annotation { "Feature Type Name" : "Feature", "Feature Type Description" : "" }
export const myFeature = defineFeature(function(context is Context, id is Id, definition is map)
    precondition{}
    {
        {
            var Q0;
            Q0=qCreatedBy(makeId("Front.planeOp"),FACE);
            var sketch = newSketch(context, id + "F0", { "sketchPlane" : qUnion([Q0])});
            skArc(sketch, "E0", {"start": v(30.48, 0) * mm, "mid": v(15.24, 7.4) * mm, "end": v(0, 0) * mm});
            skArc(sketch, "E1", {"start": v(33.68, -27.09) * mm, "mid": v(35.27, -13.17) * mm, "end": v(30.48, 0) * mm});
            skArc(sketch, "E2", {"start": v(16.38, -43.25) * mm, "mid": v(26.93, -37.2) * mm, "end": v(33.68, -27.09) * mm});
            skArc(sketch, "E3", {"start": v(0, -40) * mm, "mid": v(7.87, -43.22) * mm, "end": v(16.38, -43.25) * mm});
            skLineSegment(sketch, "E4", {"start": v(0, 0) * mm, "end": v(0, -5.57) * mm});
            skArc(sketch, "E5.0", {"start": v(28.04, -1.75) * mm, "mid": v(15.17, 4.4) * mm, "end": v(2.36, -1.86) * mm});
            skArc(sketch, "E5.1", {"start": v(30.86, -26.06) * mm, "mid": v(32.3, -13.58) * mm, "end": v(28.04, -1.75) * mm});
            skArc(sketch, "E5.2", {"start": v(15.67, -40.33) * mm, "mid": v(24.93, -34.97) * mm, "end": v(30.86, -26.06) * mm});
            skArc(sketch, "E5.3", {"start": v(0.74, -36.86) * mm, "mid": v(7.84, -40.15) * mm, "end": v(15.67, -40.33) * mm});
            skArc(sketch, "E6", {"start": v(2.36, -1.86) * mm, "mid": v(1.03, -3.62) * mm, "end": v(0, -5.57) * mm});
            skArc(sketch, "E7", {"start": v(0, -36.13) * mm, "mid": v(0.34, -36.52) * mm, "end": v(0.74, -36.86) * mm});
            skLineSegment(sketch, "E8.trimOffspring", {"start": v(0, -36.13) * mm, "end": v(0, -40) * mm});
            skArc(sketch, "E9.0", {"start": v(28.85, -1.17) * mm, "mid": v(15.2, 5.4) * mm, "end": v(1.57, -1.24) * mm});
            skArc(sketch, "E9.1", {"start": v(31.8, -26.4) * mm, "mid": v(33.29, -13.44) * mm, "end": v(28.85, -1.17) * mm});
            skArc(sketch, "E9.2", {"start": v(15.96, -41.29) * mm, "mid": v(25.62, -35.7) * mm, "end": v(31.8, -26.4) * mm});
            skSolve(sketch);
        }
        {
            var Q0;
            Q0 = qSketchRegion(id + "F0", true);
            var Q1;
            Q1=sQuery(id+"F0.wireOp",EDGE,"E4");
            revolve(context, id + "F1", {"entities" : qUnion([Q0]), "axis" : qUnion([Q1]), "revolveType" : RevolveType.FULL});
        }
        {
            var Q0;
            Q0=qCreatedBy(makeId("Top.planeOp"),FACE);
            cPlane(context, id + "F2", {"entities" : qUnion([Q0]), "cplaneType" : CPlaneType.OFFSET, "offset" : 7 * mm, "width" : 150 * mm, "height" : 150 * mm});
        }
        {
            var Q0;
            Q0=qCreatedBy(id+"F2.planeOp",FACE);
            var sketch = newSketch(context, id + "F3", { "sketchPlane" : qUnion([Q0])});
            skCircle(sketch, "E10", {"center": v(0, 0) * mm, "radius": 2.5 * mm});
            skSolve(sketch);
        }
        {
            var Q0;
            Q0=makeQuery(id+"F3.imprint","IMPRINT",FACE,{"disambiguationData":[TD([[makeQuery(id+"F3.imprint","IMPRINT",EDGE,{"derivedFrom":sQuery(id+"F3.wireOp",EDGE,"E10")}),1.0]])]});
            extrude(context, id + "F4", {"entities" : qUnion([Q0]), "operationType" : NewBodyOperationType.REMOVE, "oppositeDirection" : true, "depth" : 30 * mm});
        }
        {
            var Q0;
            Q0=qCreatedBy(makeId("Front.planeOp"),FACE);
            cPlane(context, id + "F5", {"entities" : qUnion([Q0]), "cplaneType" : CPlaneType.OFFSET, "offset" : 35.5 * mm, "width" : 150 * mm, "height" : 150 * mm});
        }
        {
            var Q0;
            Q0=qCreatedBy(id+"F5.planeOp",FACE);
            var sketch = newSketch(context, id + "F6", { "sketchPlane" : qUnion([Q0])});
            skLineSegment(sketch, "E11.bottom", {"start": v(-34.26, 0) * mm, "end": v(34.36, 0) * mm, "construction": true});
            skLineSegment(sketch, "E11.top", {"start": v(-34.26, -19.03) * mm, "end": v(34.36, -19.03) * mm, "construction": true});
            skLineSegment(sketch, "E11.left", {"start": v(-34.26, 0) * mm, "end": v(-34.26, -19.03) * mm, "construction": true});
            skLineSegment(sketch, "E11.right", {"start": v(34.36, 0) * mm, "end": v(34.36, -19.03) * mm, "construction": true});
            skText(sketch, "E12", { "text": "El Manzanito\n", "fontName": "OpenSans-Bold.ttf"});
            const initialGuessF6  = {"E12": [-0.03426, -0.01903, 1, 0, 0.00765]};
            skSetInitialGuess(sketch, initialGuessF6);
            skSolve(sketch);
        }
        {
            var Q0;
            Q0 = qSketchRegion(id + "F6", true);
            var Q1;
            Q1=makeQuery(id+"F1.opRevolve","SWEPT_FACE",FACE,{"disambiguationData":[OSD([sQuery(id+"F0.wireOp",EDGE,"E1")])]});
            extrude(context, id + "F7", {"entities" : qUnion([Q0]), "endBound" : BoundingType.UP_TO_SURFACE, "oppositeDirection" : true, "endBoundEntityFace" : qUnion([Q1]), "depth" : 25 * mm});
        }
    });